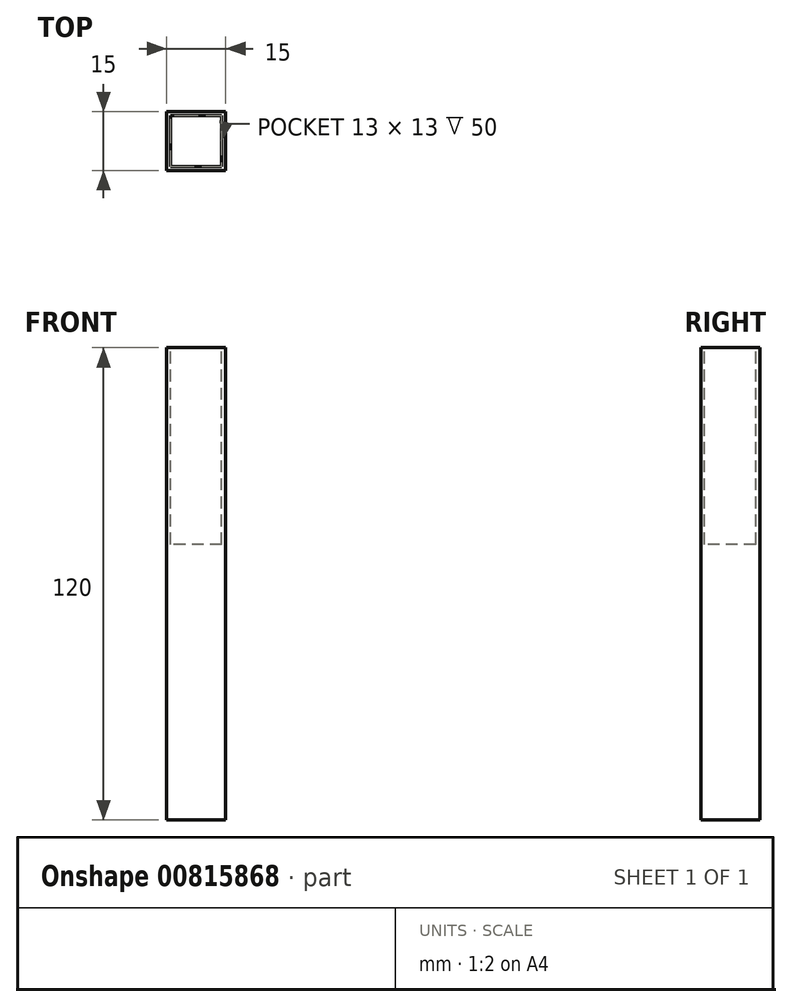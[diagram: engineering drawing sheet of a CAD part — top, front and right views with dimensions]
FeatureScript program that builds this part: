
annotation { "Feature Type Name" : "Feature", "Feature Type Description" : "" }
export const myFeature = defineFeature(function(context is Context, id is Id, definition is map)
    precondition{}
    {
        {
            var Q0;
            Q0=qCreatedBy(makeId("Top.planeOp"),FACE);
            var sketch = newSketch(context, id + "F0", { "sketchPlane" : qUnion([Q0])});
            skLineSegment(sketch, "E0.bottom", {"start": v(-7.5, 7.5) * mm, "end": v(7.5, 7.5) * mm});
            skLineSegment(sketch, "E0.top", {"start": v(-7.5, -7.5) * mm, "end": v(7.5, -7.5) * mm});
            skLineSegment(sketch, "E0.left", {"start": v(-7.5, 7.5) * mm, "end": v(-7.5, -7.5) * mm});
            skLineSegment(sketch, "E0.right", {"start": v(7.5, 7.5) * mm, "end": v(7.5, -7.5) * mm});
            skPoint(sketch, "E0.middle", {"position": v(0, 0) * mm});
            skSolve(sketch);
        }
        {
            var Q0;
            Q0 = qSketchRegion(id + "F0", true);
            extrude(context, id + "F1", {"entities" : qUnion([Q0]), "depth" : 60 * mm, "offsetDistance" : 25 * mm, "hasSecondDirection" : true, "secondDirectionOppositeDirection" : true, "secondDirectionDepth" : 60 * mm});
        }
        {
            var Q0;
            Q0=makeQuery(id+"F1.opExtrude","CAP_FACE",FACE,{"disambiguationData":[OSD([sQuery(id+"F0.wireOp",EDGE,"E0.bottom"),sQuery(id+"F0.wireOp",EDGE,"E0.top"),sQuery(id+"F0.wireOp",EDGE,"E0.left"),sQuery(id+"F0.wireOp",EDGE,"E0.right")])],"isStart":false});
            var sketch = newSketch(context, id + "F2", { "sketchPlane" : qUnion([Q0])});
            skLineSegment(sketch, "E1.bottom", {"start": v(6.5, 6.5) * mm, "end": v(-6.5, 6.5) * mm});
            skLineSegment(sketch, "E1.top", {"start": v(6.5, -6.5) * mm, "end": v(-6.5, -6.5) * mm});
            skLineSegment(sketch, "E1.left", {"start": v(6.5, 6.5) * mm, "end": v(6.5, -6.5) * mm});
            skLineSegment(sketch, "E1.right", {"start": v(-6.5, 6.5) * mm, "end": v(-6.5, -6.5) * mm});
            skPoint(sketch, "E1.middle", {"position": v(0, 0) * mm});
            skSolve(sketch);
        }
        {
            var Q0;
            Q0=makeQuery(id+"F2.imprint","IMPRINT",FACE,{"disambiguationData":[TD([[makeQuery(id+"F2.imprint","IMPRINT",EDGE,{"derivedFrom":sQuery(id+"F2.wireOp",EDGE,"E1.bottom")}),1.0]])]});
            extrude(context, id + "F3", {"entities" : qUnion([Q0]), "operationType" : NewBodyOperationType.REMOVE, "oppositeDirection" : true, "depth" : 50 * mm, "offsetDistance" : 25 * mm});
        }
    });
